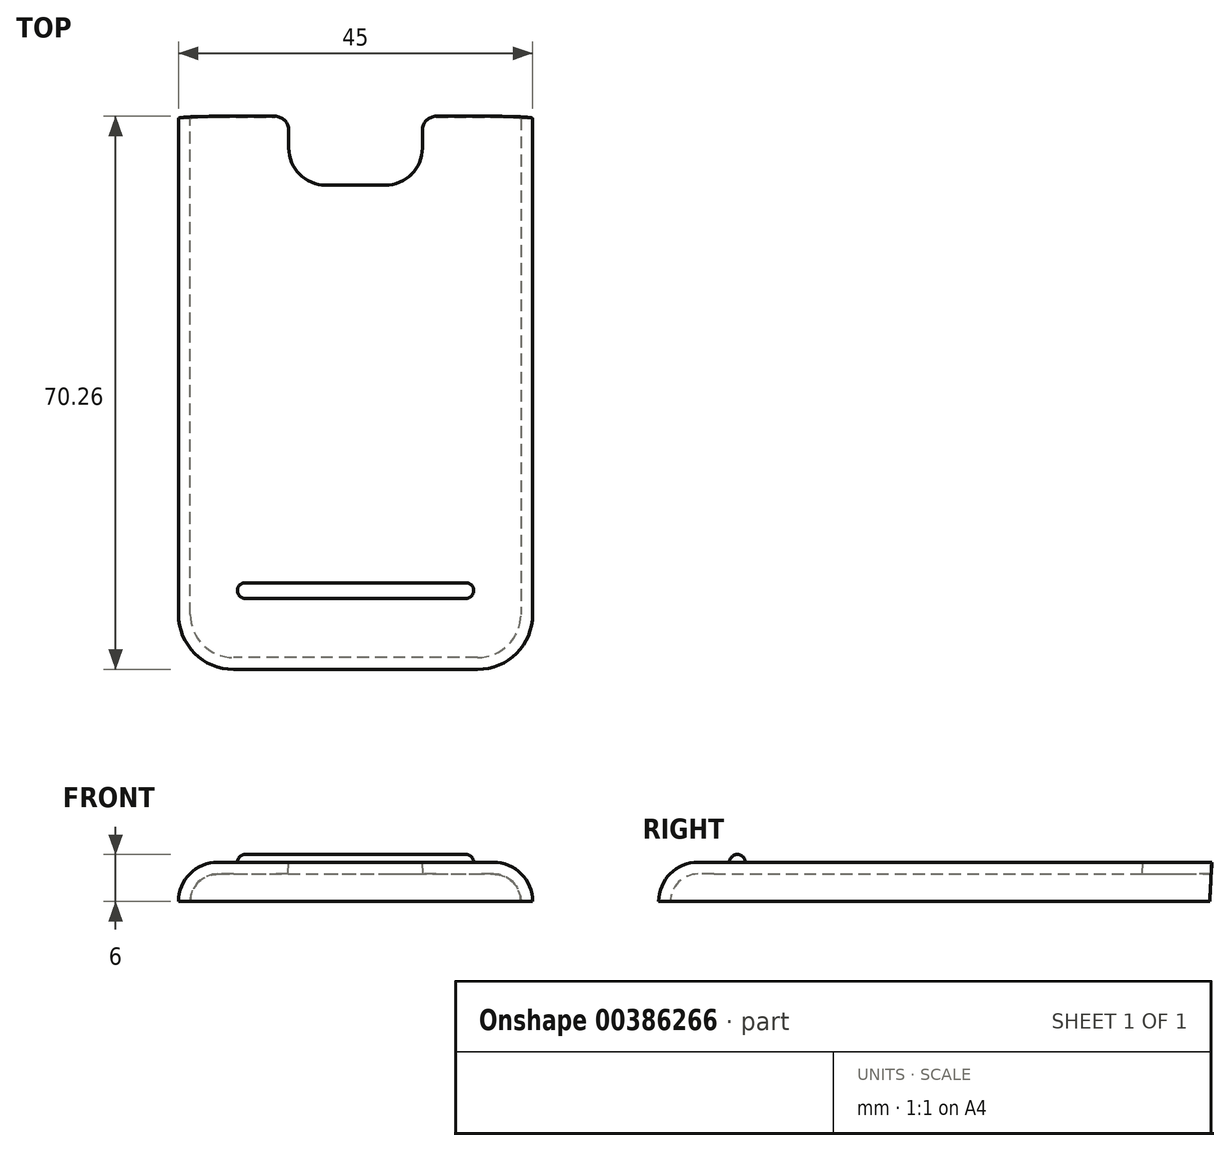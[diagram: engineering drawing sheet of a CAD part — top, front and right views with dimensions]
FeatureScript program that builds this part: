
annotation { "Feature Type Name" : "Feature", "Feature Type Description" : "" }
export const myFeature = defineFeature(function(context is Context, id is Id, definition is map)
    precondition{}
    {
        {
            var Q0;
            Q0=qCreatedBy(makeId("Top.planeOp"),FACE);
            var sketch = newSketch(context, id + "F0", { "sketchPlane" : qUnion([Q0])});
            skLineSegment(sketch, "E0.bottom", {"start": v(22.5, 35) * mm, "end": v(10.25, 35) * mm});
            skLineSegment(sketch, "E0.top", {"start": v(15.5, -35) * mm, "end": v(-15.5, -35) * mm});
            skLineSegment(sketch, "E0.left", {"start": v(22.5, 35) * mm, "end": v(22.5, -28) * mm});
            skLineSegment(sketch, "E0.right", {"start": v(-22.5, 35) * mm, "end": v(-22.5, -28) * mm});
            skPoint(sketch, "E0.middle", {"position": v(0, 0) * mm});
            skPoint(sketch, "E1.visualSharp", {"position": v(-22.5, -35) * mm});
            skArc(sketch, "E1.filletArc", {"start": v(-22.5, -28) * mm, "mid": v(-20.45, -32.95) * mm, "end": v(-15.5, -35) * mm});
            skPoint(sketch, "E2.visualSharp", {"position": v(22.5, -35) * mm});
            skArc(sketch, "E2.filletArc", {"start": v(15.5, -35) * mm, "mid": v(20.45, -32.95) * mm, "end": v(22.5, -28) * mm});
            skLineSegment(sketch, "E3.bottom", {"start": v(-3.75, 26.25) * mm, "end": v(3.75, 26.25) * mm});
            skLineSegment(sketch, "E3.left", {"start": v(-8.75, 31.25) * mm, "end": v(-8.75, 33.5) * mm});
            skLineSegment(sketch, "E3.right", {"start": v(8.75, 31.25) * mm, "end": v(8.75, 33.5) * mm});
            skPoint(sketch, "E3.middle", {"position": v(0, 35) * mm});
            skPoint(sketch, "E4.orphan", {"position": v(8.75, 43.75) * mm});
            skPoint(sketch, "E5.orphan", {"position": v(-8.75, 43.75) * mm});
            skLineSegment(sketch, "E6.trimOffspring", {"start": v(-10.25, 35) * mm, "end": v(-22.5, 35) * mm});
            skPoint(sketch, "E7.visualSharp", {"position": v(-8.75, 35) * mm});
            skArc(sketch, "E7.filletArc", {"start": v(-8.75, 33.5) * mm, "mid": v(-9.19, 34.56) * mm, "end": v(-10.25, 35) * mm});
            skPoint(sketch, "E8.visualSharp", {"position": v(8.75, 35) * mm});
            skArc(sketch, "E8.filletArc", {"start": v(10.25, 35) * mm, "mid": v(9.19, 34.56) * mm, "end": v(8.75, 33.5) * mm});
            skPoint(sketch, "E9.visualSharp", {"position": v(-8.75, 26.25) * mm});
            skArc(sketch, "E9.filletArc", {"start": v(-8.75, 31.25) * mm, "mid": v(-7.29, 27.71) * mm, "end": v(-3.75, 26.25) * mm});
            skPoint(sketch, "E10.visualSharp", {"position": v(8.75, 26.25) * mm});
            skArc(sketch, "E10.filletArc", {"start": v(3.75, 26.25) * mm, "mid": v(7.29, 27.71) * mm, "end": v(8.75, 31.25) * mm});
            skSolve(sketch);
        }
        {
            var Q0;
            Q0=makeQuery(id+"F0.imprint","IMPRINT",FACE,{"disambiguationData":[TD([[makeQuery(id+"F0.imprint","IMPRINT",EDGE,{"derivedFrom":sQuery(id+"F0.wireOp",EDGE,"E0.bottom")}),1.0]])]});
            extrude(context, id + "F1", {"entities" : qUnion([Q0]), "depth" : 5 * mm, "hasDraft" : true, "draftAngle" : 3 * degree});
        }
        {
            var Q0;
            Q0=makeQuery(id+"F1.opExtrude","CAP_EDGE",EDGE,{"disambiguationData":[OSD([sQuery(id+"F0.wireOp",EDGE,"E0.left")])],"isStart":false});
            fillet(context, id + "F2", {"entities" : qUnion([Q0]), "radius" : 5 * mm, "tangentPropagation" : true, "allowEdgeOverflow" : false});
        }
        {
            var Q0;
            Q0=makeQuery(id+"F1.opExtrude","CAP_FACE",FACE,{"disambiguationData":[OSD([sQuery(id+"F0.wireOp",EDGE,"E0.bottom"),sQuery(id+"F0.wireOp",EDGE,"E0.top"),sQuery(id+"F0.wireOp",EDGE,"E0.left"),sQuery(id+"F0.wireOp",EDGE,"E0.right"),sQuery(id+"F0.wireOp",EDGE,"E1.filletArc"),sQuery(id+"F0.wireOp",EDGE,"E2.filletArc"),sQuery(id+"F0.wireOp",EDGE,"E3.bottom"),sQuery(id+"F0.wireOp",EDGE,"E3.left"),sQuery(id+"F0.wireOp",EDGE,"E3.right"),sQuery(id+"F0.wireOp",EDGE,"E6.trimOffspring"),sQuery(id+"F0.wireOp",EDGE,"E7.filletArc"),sQuery(id+"F0.wireOp",EDGE,"E8.filletArc"),sQuery(id+"F0.wireOp",EDGE,"E9.filletArc"),sQuery(id+"F0.wireOp",EDGE,"E10.filletArc")])],"isStart":true});
            var Q1;
            Q1=makeQuery(id+"F1.opExtrude","SWEPT_FACE",FACE,{"disambiguationData":[OSD([sQuery(id+"F0.wireOp",EDGE,"E0.bottom")])]});
            var Q2;
            Q2=makeQuery(id+"F1.opExtrude","SWEPT_FACE",FACE,{"disambiguationData":[OSD([sQuery(id+"F0.wireOp",EDGE,"E8.filletArc")])]});
            var Q3;
            Q3=makeQuery(id+"F1.opExtrude","SWEPT_FACE",FACE,{"disambiguationData":[OSD([sQuery(id+"F0.wireOp",EDGE,"E3.right")])]});
            var Q4;
            Q4=makeQuery(id+"F1.opExtrude","SWEPT_FACE",FACE,{"disambiguationData":[OSD([sQuery(id+"F0.wireOp",EDGE,"E10.filletArc")])]});
            var Q5;
            Q5=makeQuery(id+"F1.opExtrude","SWEPT_FACE",FACE,{"disambiguationData":[OSD([sQuery(id+"F0.wireOp",EDGE,"E3.bottom")])]});
            var Q6;
            Q6=makeQuery(id+"F1.opExtrude","SWEPT_FACE",FACE,{"disambiguationData":[OSD([sQuery(id+"F0.wireOp",EDGE,"E6.trimOffspring")])]});
            var Q7;
            Q7=makeQuery(id+"F1.opExtrude","SWEPT_FACE",FACE,{"disambiguationData":[OSD([sQuery(id+"F0.wireOp",EDGE,"E7.filletArc")])]});
            var Q8;
            Q8=makeQuery(id+"F1.opExtrude","SWEPT_FACE",FACE,{"disambiguationData":[OSD([sQuery(id+"F0.wireOp",EDGE,"E9.filletArc")])]});
            var Q9;
            Q9=makeQuery(id+"F1.opExtrude","SWEPT_FACE",FACE,{"disambiguationData":[OSD([sQuery(id+"F0.wireOp",EDGE,"E3.left")])]});
            shell(context, id + "F3", {"entities" : qUnion([Q0, Q1, Q2, Q3, Q4, Q5, Q6, Q7, Q8, Q9]), "thickness" : 1.5 * mm});
        }
        {
            var Q0;
            Q0=makeQuery(id+"F1.opExtrude","CAP_FACE",FACE,{"disambiguationData":[OSD([sQuery(id+"F0.wireOp",EDGE,"E0.bottom"),sQuery(id+"F0.wireOp",EDGE,"E0.top"),sQuery(id+"F0.wireOp",EDGE,"E0.left"),sQuery(id+"F0.wireOp",EDGE,"E0.right"),sQuery(id+"F0.wireOp",EDGE,"E1.filletArc"),sQuery(id+"F0.wireOp",EDGE,"E2.filletArc"),sQuery(id+"F0.wireOp",EDGE,"E3.bottom"),sQuery(id+"F0.wireOp",EDGE,"E3.left"),sQuery(id+"F0.wireOp",EDGE,"E3.right"),sQuery(id+"F0.wireOp",EDGE,"E6.trimOffspring"),sQuery(id+"F0.wireOp",EDGE,"E7.filletArc"),sQuery(id+"F0.wireOp",EDGE,"E8.filletArc"),sQuery(id+"F0.wireOp",EDGE,"E9.filletArc"),sQuery(id+"F0.wireOp",EDGE,"E10.filletArc")])],"isStart":false});
            var sketch = newSketch(context, id + "F4", { "sketchPlane" : qUnion([Q0])});
            skLineSegment(sketch, "E11.bottom", {"start": v(15, -24) * mm, "end": v(-15, -24) * mm});
            skLineSegment(sketch, "E11.top", {"start": v(15, -26) * mm, "end": v(-15, -26) * mm});
            skLineSegment(sketch, "E11.left", {"start": v(15, -24) * mm, "end": v(15, -26) * mm});
            skLineSegment(sketch, "E11.right", {"start": v(-15, -24) * mm, "end": v(-15, -26) * mm});
            skPoint(sketch, "E11.middle", {"position": v(0, -25) * mm});
            skPoint(sketch, "E11.middle.positionSnap0", {"position": v(0, -30) * mm});
            skPoint(sketch, "E11.centerSnap0", {"position": v(0, -30) * mm});
            skSolve(sketch);
        }
        {
            var Q0;
            Q0 = qSketchRegion(id + "F4", true);
            extrude(context, id + "F5", {"entities" : qUnion([Q0]), "operationType" : NewBodyOperationType.ADD, "depth" : 1 * mm});
        }
        {
            var Q0;
            Q0=makeQuery(id+"F5.opExtrude","SWEPT_EDGE",EDGE,{"disambiguationData":[OSD([sQuery(id+"F4.wireOp",EDGE,"E11.top"),sQuery(id+"F4.wireOp",EDGE,"E11.left")])]});
            var Q1;
            Q1=makeQuery(id+"F5.opExtrude","SWEPT_EDGE",EDGE,{"disambiguationData":[OSD([sQuery(id+"F4.wireOp",EDGE,"E11.bottom"),sQuery(id+"F4.wireOp",EDGE,"E11.left")])]});
            var Q2;
            Q2=makeQuery(id+"F5.opExtrude","SWEPT_EDGE",EDGE,{"disambiguationData":[OSD([sQuery(id+"F4.wireOp",EDGE,"E11.bottom"),sQuery(id+"F4.wireOp",EDGE,"E11.right")])]});
            var Q3;
            Q3=makeQuery(id+"F5.opExtrude","SWEPT_EDGE",EDGE,{"disambiguationData":[OSD([sQuery(id+"F4.wireOp",EDGE,"E11.top"),sQuery(id+"F4.wireOp",EDGE,"E11.right")])]});
            fillet(context, id + "F6", {"entities" : qUnion([Q0, Q1, Q2, Q3]), "radius" : 1 * mm, "tangentPropagation" : true, "allowEdgeOverflow" : false});
        }
        {
            var Q0;
            Q0=makeQuery(id+"F5.opExtrude","CAP_FACE",FACE,{"disambiguationData":[OSD([sQuery(id+"F4.wireOp",EDGE,"E11.bottom"),sQuery(id+"F4.wireOp",EDGE,"E11.top"),sQuery(id+"F4.wireOp",EDGE,"E11.left"),sQuery(id+"F4.wireOp",EDGE,"E11.right")])],"isStart":false});
            fillet(context, id + "F7", {"entities" : qUnion([Q0]), "radius" : 1 * mm, "tangentPropagation" : true, "allowEdgeOverflow" : false});
        }
    });
